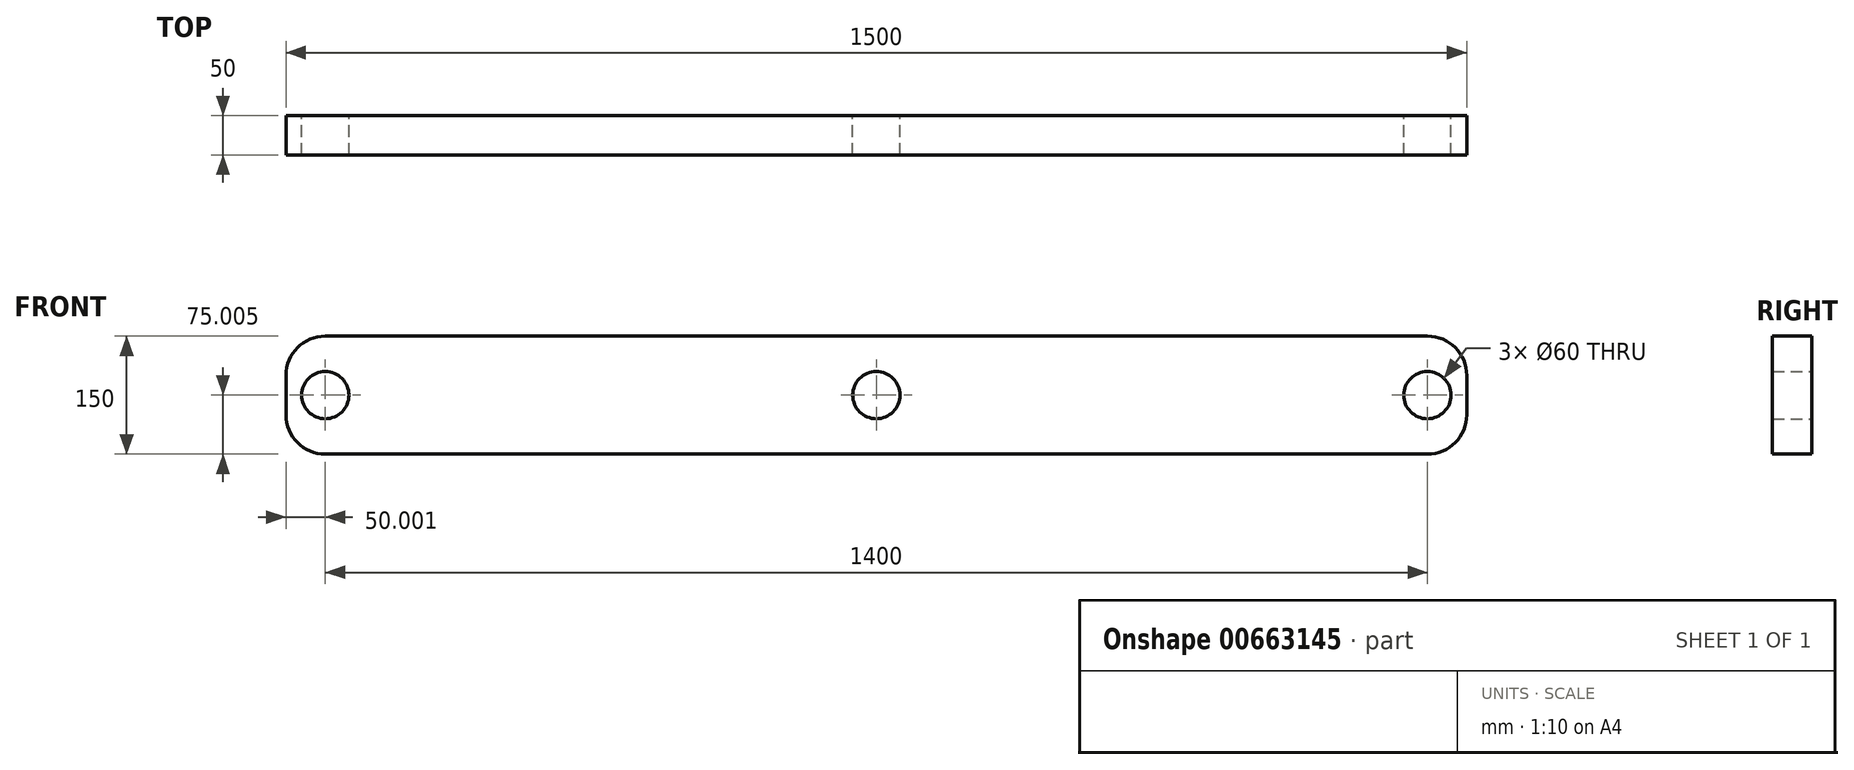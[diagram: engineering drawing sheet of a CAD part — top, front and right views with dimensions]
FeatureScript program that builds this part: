
annotation { "Feature Type Name" : "Feature", "Feature Type Description" : "" }
export const myFeature = defineFeature(function(context is Context, id is Id, definition is map)
    precondition{}
    {
        {
            var Q0;
            Q0=qCreatedBy(makeId("Front.planeOp"),FACE);
            var sketch = newSketch(context, id + "F0", { "sketchPlane" : qUnion([Q0])});
            skLineSegment(sketch, "E0", {"start": v(1025.43, 431.4) * mm, "end": v(-474.57, 431.4) * mm});
            skLineSegment(sketch, "E1", {"start": v(-474.57, 431.4) * mm, "end": v(-474.57, 281.4) * mm});
            skLineSegment(sketch, "E2", {"start": v(-474.57, 281.4) * mm, "end": v(1025.43, 281.4) * mm});
            skLineSegment(sketch, "E3", {"start": v(1025.43, 281.4) * mm, "end": v(1025.43, 431.4) * mm});
            skCircle(sketch, "E4", {"center": v(-424.57, 356.4) * mm, "radius": 30 * mm});
            skCircle(sketch, "E5", {"center": v(975.43, 356.4) * mm, "radius": 30 * mm});
            skCircle(sketch, "E6", {"center": v(275.43, 356.4) * mm, "radius": 30 * mm});
            skSolve(sketch);
        }
        {
            var Q0;
            Q0 = qSketchRegion(id + "F0", true);
            extrude(context, id + "F1", {"entities" : qUnion([Q0]), "depth" : 50 * mm, "offsetDistance" : 25 * mm});
        }
        {
            var Q0;
            Q0=makeQuery(id+"F1.opExtrude","SWEPT_EDGE",EDGE,{"disambiguationData":[OSD([sQuery(id+"F0.wireOp",EDGE,"E0"),sQuery(id+"F0.wireOp",EDGE,"E1")])]});
            var Q1;
            Q1=makeQuery(id+"F1.opExtrude","SWEPT_EDGE",EDGE,{"disambiguationData":[OSD([sQuery(id+"F0.wireOp",EDGE,"E1"),sQuery(id+"F0.wireOp",EDGE,"E2")])]});
            var Q2;
            Q2=makeQuery(id+"F1.opExtrude","SWEPT_EDGE",EDGE,{"disambiguationData":[OSD([sQuery(id+"F0.wireOp",EDGE,"E0"),sQuery(id+"F0.wireOp",EDGE,"E3")])]});
            var Q3;
            Q3=makeQuery(id+"F1.opExtrude","SWEPT_EDGE",EDGE,{"disambiguationData":[OSD([sQuery(id+"F0.wireOp",EDGE,"E2"),sQuery(id+"F0.wireOp",EDGE,"E3")])]});
            fillet(context, id + "F2", {"entities" : qUnion([Q0, Q1, Q2, Q3]), "radius" : 50 * mm, "tangentPropagation" : true, "allowEdgeOverflow" : false});
        }
    });
